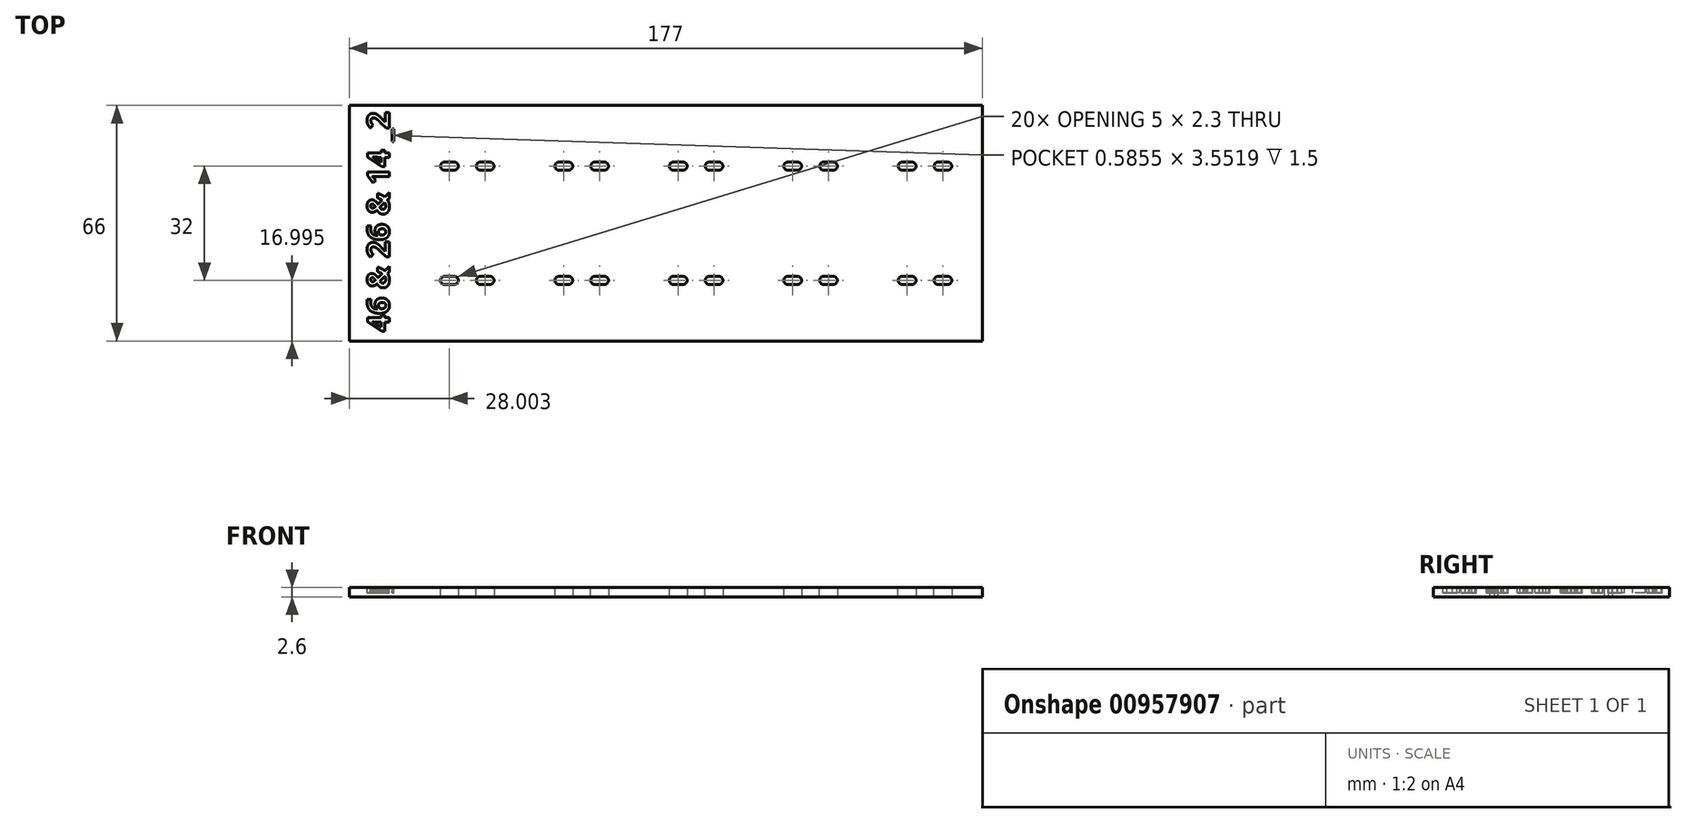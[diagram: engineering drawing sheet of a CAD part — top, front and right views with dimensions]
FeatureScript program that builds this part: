
annotation { "Feature Type Name" : "Feature", "Feature Type Description" : "" }
export const myFeature = defineFeature(function(context is Context, id is Id, definition is map)
    precondition{}
    {
        {
            var Q0;
            Q0=qCreatedBy(makeId("Top.planeOp"),FACE);
            var sketch = newSketch(context, id + "F0", { "sketchPlane" : qUnion([Q0])});
            skLineSegment(sketch, "E0.bottom", {"start": v(-87.55, 16.72) * mm, "end": v(89.45, 16.72) * mm});
            skLineSegment(sketch, "E0.top", {"start": v(-87.55, -49.28) * mm, "end": v(89.45, -49.28) * mm});
            skLineSegment(sketch, "E0.left", {"start": v(-87.55, 16.72) * mm, "end": v(-87.55, -49.28) * mm});
            skLineSegment(sketch, "E0.right", {"start": v(89.45, 16.72) * mm, "end": v(89.45, -49.28) * mm});
            skSolve(sketch);
        }
        {
            var Q0;
            Q0=makeQuery(id+"F0.imprint","IMPRINT",FACE,{"disambiguationData":[TD([[makeQuery(id+"F0.imprint","IMPRINT",EDGE,{"derivedFrom":sQuery(id+"F0.wireOp",EDGE,"E0.bottom")}),-1.0]])]});
            extrude(context, id + "F1", {"entities" : qUnion([Q0]), "depth" : 2.6 * mm, "offsetDistance" : 25 * mm});
        }
        {
            var Q0;
            Q0=makeQuery(id+"F1.opExtrude","CAP_FACE",FACE,{"disambiguationData":[OSD([sQuery(id+"F0.wireOp",EDGE,"E0.bottom"),sQuery(id+"F0.wireOp",EDGE,"E0.top"),sQuery(id+"F0.wireOp",EDGE,"E0.left"),sQuery(id+"F0.wireOp",EDGE,"E0.right")])],"isStart":false});
            var sketch = newSketch(context, id + "F2", { "sketchPlane" : qUnion([Q0])});
            skText(sketch, "E1", { "text": "46 & 26 & 14 _2", "fontName": "OpenSans-Bold.ttf"});
            const initialGuessF2  = {"E1": [-0.0764, -0.0467, 0, 1, 0.00616]};
            skSetInitialGuess(sketch, initialGuessF2);
            skSolve(sketch);
        }
        {
            var Q0;
            Q0=qSketchRegion(id+"F2",true);
            extrude(context, id + "F3", {"entities" : qUnion([Q0]), "operationType" : NewBodyOperationType.REMOVE, "oppositeDirection" : true, "depth" : 1.5 * mm, "offsetDistance" : 25 * mm});
        }
        {
            var Q0;
            {var subQ0=sQuery(id+"F0.wireOp",EDGE,"E0.left");var subQ1=sQuery(id+"F0.wireOp",EDGE,"E0.bottom");var subQ2=sQuery(id+"F0.wireOp",EDGE,"E0.right");var subQ3=sQuery(id+"F0.wireOp",EDGE,"E0.top");Q0=makeQuery(id+"F3.boolean.opBoolean","SPLIT",FACE,{"disambiguationData":[TD([makeQuery(id+"F1.opExtrude","SWEPT_FACE",FACE,{"disambiguationData":[OSD([subQ1])]})])],"derivedFrom":makeQuery(id+"F1.opExtrude","CAP_FACE",FACE,{"disambiguationData":[OSD([subQ1,subQ3,subQ0,subQ2])],"isStart":false})});}
            var sketch = newSketch(context, id + "F4", { "sketchPlane" : qUnion([Q0])});
            skCircle(sketch, "E2", {"center": v(-59.55, -0.28) * mm, "radius": 1.15 * mm});
            skCircle(sketch, "E3", {"center": v(-49.55, -0.28) * mm, "radius": 1.15 * mm});
            skCircle(sketch, "E4", {"center": v(-27.55, -0.28) * mm, "radius": 1.15 * mm});
            skCircle(sketch, "E5", {"center": v(-17.55, -0.28) * mm, "radius": 1.15 * mm});
            skCircle(sketch, "E6", {"center": v(4.45, -0.28) * mm, "radius": 1.15 * mm});
            skCircle(sketch, "E7", {"center": v(14.45, -0.28) * mm, "radius": 1.15 * mm});
            skCircle(sketch, "E8", {"center": v(36.45, -0.28) * mm, "radius": 1.15 * mm});
            skCircle(sketch, "E9", {"center": v(46.45, -0.28) * mm, "radius": 1.15 * mm});
            skCircle(sketch, "E10", {"center": v(68.45, -0.28) * mm, "radius": 1.15 * mm});
            skCircle(sketch, "E11", {"center": v(78.45, -0.28) * mm, "radius": 1.15 * mm});
            skCircle(sketch, "E12", {"center": v(-59.55, -32.28) * mm, "radius": 1.15 * mm});
            skCircle(sketch, "E13", {"center": v(-49.55, -32.28) * mm, "radius": 1.15 * mm});
            skCircle(sketch, "E14", {"center": v(-27.55, -32.28) * mm, "radius": 1.15 * mm});
            skCircle(sketch, "E15", {"center": v(-17.55, -32.28) * mm, "radius": 1.15 * mm});
            skCircle(sketch, "E16", {"center": v(4.45, -32.28) * mm, "radius": 1.15 * mm});
            skCircle(sketch, "E17", {"center": v(14.45, -32.28) * mm, "radius": 1.15 * mm});
            skCircle(sketch, "E18", {"center": v(36.45, -32.28) * mm, "radius": 1.15 * mm});
            skCircle(sketch, "E19", {"center": v(46.45, -32.28) * mm, "radius": 1.15 * mm});
            skCircle(sketch, "E20", {"center": v(68.45, -32.28) * mm, "radius": 1.15 * mm});
            skCircle(sketch, "E21", {"center": v(78.45, -32.28) * mm, "radius": 1.15 * mm});
            skLineSegment(sketch, "E22.bottom", {"start": v(-62.05, -31.13) * mm, "end": v(-57.05, -31.13) * mm});
            skLineSegment(sketch, "E22.top", {"start": v(-62.05, -33.43) * mm, "end": v(-57.05, -33.43) * mm});
            skLineSegment(sketch, "E22.left", {"start": v(-62.05, -31.13) * mm, "end": v(-62.05, -33.43) * mm});
            skLineSegment(sketch, "E22.right", {"start": v(-57.05, -31.13) * mm, "end": v(-57.05, -33.43) * mm});
            skLineSegment(sketch, "E23.bottom", {"start": v(-62.05, 0.87) * mm, "end": v(-57.05, 0.87) * mm});
            skLineSegment(sketch, "E23.top", {"start": v(-62.05, -1.43) * mm, "end": v(-57.05, -1.43) * mm});
            skLineSegment(sketch, "E23.left", {"start": v(-62.05, 0.87) * mm, "end": v(-62.05, -1.43) * mm});
            skLineSegment(sketch, "E23.right", {"start": v(-57.05, 0.87) * mm, "end": v(-57.05, -1.43) * mm});
            skLineSegment(sketch, "E24.bottom", {"start": v(-52.05, 0.87) * mm, "end": v(-47.05, 0.87) * mm});
            skLineSegment(sketch, "E24.top", {"start": v(-52.05, -1.43) * mm, "end": v(-47.05, -1.43) * mm});
            skLineSegment(sketch, "E24.left", {"start": v(-52.05, 0.87) * mm, "end": v(-52.05, -1.43) * mm});
            skLineSegment(sketch, "E24.right", {"start": v(-47.05, 0.87) * mm, "end": v(-47.05, -1.43) * mm});
            skLineSegment(sketch, "E25.bottom", {"start": v(-30.05, 0.87) * mm, "end": v(-25.05, 0.87) * mm});
            skLineSegment(sketch, "E25.top", {"start": v(-30.05, -1.43) * mm, "end": v(-25.05, -1.43) * mm});
            skLineSegment(sketch, "E25.left", {"start": v(-30.05, 0.87) * mm, "end": v(-30.05, -1.43) * mm});
            skLineSegment(sketch, "E25.right", {"start": v(-25.05, 0.87) * mm, "end": v(-25.05, -1.43) * mm});
            skLineSegment(sketch, "E26.bottom", {"start": v(-20.05, 0.87) * mm, "end": v(-15.05, 0.87) * mm});
            skLineSegment(sketch, "E26.top", {"start": v(-20.05, -1.43) * mm, "end": v(-15.05, -1.43) * mm});
            skLineSegment(sketch, "E26.left", {"start": v(-20.05, 0.87) * mm, "end": v(-20.05, -1.43) * mm});
            skLineSegment(sketch, "E26.right", {"start": v(-15.05, 0.87) * mm, "end": v(-15.05, -1.43) * mm});
            skLineSegment(sketch, "E27.bottom", {"start": v(1.95, 0.87) * mm, "end": v(6.95, 0.87) * mm});
            skLineSegment(sketch, "E27.top", {"start": v(1.95, -1.43) * mm, "end": v(6.95, -1.43) * mm});
            skLineSegment(sketch, "E27.left", {"start": v(1.95, 0.87) * mm, "end": v(1.95, -1.43) * mm});
            skLineSegment(sketch, "E27.right", {"start": v(6.95, 0.87) * mm, "end": v(6.95, -1.43) * mm});
            skLineSegment(sketch, "E28.bottom", {"start": v(11.95, 0.87) * mm, "end": v(16.95, 0.87) * mm});
            skLineSegment(sketch, "E28.top", {"start": v(11.95, -1.43) * mm, "end": v(16.95, -1.43) * mm});
            skLineSegment(sketch, "E28.left", {"start": v(11.95, 0.87) * mm, "end": v(11.95, -1.43) * mm});
            skLineSegment(sketch, "E28.right", {"start": v(16.95, 0.87) * mm, "end": v(16.95, -1.43) * mm});
            skLineSegment(sketch, "E29.bottom", {"start": v(33.95, 0.87) * mm, "end": v(38.95, 0.87) * mm});
            skLineSegment(sketch, "E29.top", {"start": v(33.95, -1.43) * mm, "end": v(38.95, -1.43) * mm});
            skLineSegment(sketch, "E29.left", {"start": v(33.95, 0.87) * mm, "end": v(33.95, -1.43) * mm});
            skLineSegment(sketch, "E29.right", {"start": v(38.95, 0.87) * mm, "end": v(38.95, -1.43) * mm});
            skLineSegment(sketch, "E30.bottom", {"start": v(43.95, 0.87) * mm, "end": v(48.95, 0.87) * mm});
            skLineSegment(sketch, "E30.top", {"start": v(43.95, -1.43) * mm, "end": v(48.95, -1.43) * mm});
            skLineSegment(sketch, "E30.left", {"start": v(43.95, 0.87) * mm, "end": v(43.95, -1.43) * mm});
            skLineSegment(sketch, "E30.right", {"start": v(48.95, 0.87) * mm, "end": v(48.95, -1.43) * mm});
            skLineSegment(sketch, "E31.bottom", {"start": v(65.95, 0.87) * mm, "end": v(70.95, 0.87) * mm});
            skLineSegment(sketch, "E31.top", {"start": v(65.95, -1.43) * mm, "end": v(70.95, -1.43) * mm});
            skLineSegment(sketch, "E31.left", {"start": v(65.95, 0.87) * mm, "end": v(65.95, -1.43) * mm});
            skLineSegment(sketch, "E31.right", {"start": v(70.95, 0.87) * mm, "end": v(70.95, -1.43) * mm});
            skLineSegment(sketch, "E32.bottom", {"start": v(75.95, 0.87) * mm, "end": v(80.95, 0.87) * mm});
            skLineSegment(sketch, "E32.top", {"start": v(75.95, -1.43) * mm, "end": v(80.95, -1.43) * mm});
            skLineSegment(sketch, "E32.left", {"start": v(75.95, 0.87) * mm, "end": v(75.95, -1.43) * mm});
            skLineSegment(sketch, "E32.right", {"start": v(80.95, 0.87) * mm, "end": v(80.95, -1.43) * mm});
            skLineSegment(sketch, "E33.bottom", {"start": v(-52.05, -31.13) * mm, "end": v(-47.05, -31.13) * mm});
            skLineSegment(sketch, "E33.top", {"start": v(-52.05, -33.43) * mm, "end": v(-47.05, -33.43) * mm});
            skLineSegment(sketch, "E33.left", {"start": v(-52.05, -31.13) * mm, "end": v(-52.05, -33.43) * mm});
            skLineSegment(sketch, "E33.right", {"start": v(-47.05, -31.13) * mm, "end": v(-47.05, -33.43) * mm});
            skLineSegment(sketch, "E34.bottom", {"start": v(-30.05, -31.13) * mm, "end": v(-25.05, -31.13) * mm});
            skLineSegment(sketch, "E34.top", {"start": v(-30.05, -33.43) * mm, "end": v(-25.05, -33.43) * mm});
            skLineSegment(sketch, "E34.left", {"start": v(-30.05, -31.13) * mm, "end": v(-30.05, -33.43) * mm});
            skLineSegment(sketch, "E34.right", {"start": v(-25.05, -31.13) * mm, "end": v(-25.05, -33.43) * mm});
            skLineSegment(sketch, "E35.bottom", {"start": v(-20.05, -31.13) * mm, "end": v(-15.05, -31.13) * mm});
            skLineSegment(sketch, "E35.top", {"start": v(-20.05, -33.43) * mm, "end": v(-15.05, -33.43) * mm});
            skLineSegment(sketch, "E35.left", {"start": v(-20.05, -31.13) * mm, "end": v(-20.05, -33.43) * mm});
            skLineSegment(sketch, "E35.right", {"start": v(-15.05, -31.13) * mm, "end": v(-15.05, -33.43) * mm});
            skLineSegment(sketch, "E36.bottom", {"start": v(1.95, -31.13) * mm, "end": v(6.95, -31.13) * mm});
            skLineSegment(sketch, "E36.top", {"start": v(1.95, -33.43) * mm, "end": v(6.95, -33.43) * mm});
            skLineSegment(sketch, "E36.left", {"start": v(1.95, -31.13) * mm, "end": v(1.95, -33.43) * mm});
            skLineSegment(sketch, "E36.right", {"start": v(6.95, -31.13) * mm, "end": v(6.95, -33.43) * mm});
            skLineSegment(sketch, "E37.bottom", {"start": v(11.95, -31.13) * mm, "end": v(16.95, -31.13) * mm});
            skLineSegment(sketch, "E37.top", {"start": v(11.95, -33.43) * mm, "end": v(16.95, -33.43) * mm});
            skLineSegment(sketch, "E37.left", {"start": v(11.95, -31.13) * mm, "end": v(11.95, -33.43) * mm});
            skLineSegment(sketch, "E37.right", {"start": v(16.95, -31.13) * mm, "end": v(16.95, -33.43) * mm});
            skLineSegment(sketch, "E38.bottom", {"start": v(33.95, -31.13) * mm, "end": v(38.95, -31.13) * mm});
            skLineSegment(sketch, "E38.top", {"start": v(33.95, -33.43) * mm, "end": v(38.95, -33.43) * mm});
            skLineSegment(sketch, "E38.left", {"start": v(33.95, -31.13) * mm, "end": v(33.95, -33.43) * mm});
            skLineSegment(sketch, "E38.right", {"start": v(38.95, -31.13) * mm, "end": v(38.95, -33.43) * mm});
            skLineSegment(sketch, "E39.bottom", {"start": v(43.95, -31.13) * mm, "end": v(48.95, -31.13) * mm});
            skLineSegment(sketch, "E39.top", {"start": v(43.95, -33.43) * mm, "end": v(48.95, -33.43) * mm});
            skLineSegment(sketch, "E39.left", {"start": v(43.95, -31.13) * mm, "end": v(43.95, -33.43) * mm});
            skLineSegment(sketch, "E39.right", {"start": v(48.95, -31.13) * mm, "end": v(48.95, -33.43) * mm});
            skLineSegment(sketch, "E40.bottom", {"start": v(65.95, -31.13) * mm, "end": v(70.95, -31.13) * mm});
            skLineSegment(sketch, "E40.top", {"start": v(65.95, -33.43) * mm, "end": v(70.95, -33.43) * mm});
            skLineSegment(sketch, "E40.left", {"start": v(65.95, -31.13) * mm, "end": v(65.95, -33.43) * mm});
            skLineSegment(sketch, "E40.right", {"start": v(70.95, -31.13) * mm, "end": v(70.95, -33.43) * mm});
            skLineSegment(sketch, "E41.bottom", {"start": v(75.95, -31.13) * mm, "end": v(80.95, -31.13) * mm});
            skLineSegment(sketch, "E41.top", {"start": v(75.95, -33.43) * mm, "end": v(80.95, -33.43) * mm});
            skLineSegment(sketch, "E41.left", {"start": v(75.95, -31.13) * mm, "end": v(75.95, -33.43) * mm});
            skLineSegment(sketch, "E41.right", {"start": v(80.95, -31.13) * mm, "end": v(80.95, -33.43) * mm});
            skSolve(sketch);
        }
        {
            var Q0;
            Q0=qSketchRegion(id+"F4",true);
            extrude(context, id + "F5", {"entities" : qUnion([Q0]), "operationType" : NewBodyOperationType.REMOVE, "endBound" : BoundingType.UP_TO_NEXT, "oppositeDirection" : true, "depth" : 25 * mm, "offsetDistance" : 25 * mm});
        }
        {
            var Q0;
            Q0=makeQuery(id+"F5.boolean.opBoolean","COPY",EDGE,{"derivedFrom":makeQuery(id+"F5.opExtrude","SWEPT_EDGE",EDGE,{"disambiguationData":[OSD([sQuery(id+"F4.wireOp",EDGE,"E23.bottom"),sQuery(id+"F4.wireOp",EDGE,"E23.left")])]})});
            var Q1;
            Q1=makeQuery(id+"F5.boolean.opBoolean","COPY",EDGE,{"derivedFrom":makeQuery(id+"F5.opExtrude","SWEPT_EDGE",EDGE,{"disambiguationData":[OSD([sQuery(id+"F4.wireOp",EDGE,"E24.bottom"),sQuery(id+"F4.wireOp",EDGE,"E24.left")])]})});
            var Q2;
            Q2=makeQuery(id+"F5.boolean.opBoolean","COPY",EDGE,{"derivedFrom":makeQuery(id+"F5.opExtrude","SWEPT_EDGE",EDGE,{"disambiguationData":[OSD([sQuery(id+"F4.wireOp",EDGE,"E25.bottom"),sQuery(id+"F4.wireOp",EDGE,"E25.left")])]})});
            var Q3;
            Q3=makeQuery(id+"F5.boolean.opBoolean","COPY",EDGE,{"derivedFrom":makeQuery(id+"F5.opExtrude","SWEPT_EDGE",EDGE,{"disambiguationData":[OSD([sQuery(id+"F4.wireOp",EDGE,"E26.bottom"),sQuery(id+"F4.wireOp",EDGE,"E26.left")])]})});
            var Q4;
            Q4=makeQuery(id+"F5.boolean.opBoolean","COPY",EDGE,{"derivedFrom":makeQuery(id+"F5.opExtrude","SWEPT_EDGE",EDGE,{"disambiguationData":[OSD([sQuery(id+"F4.wireOp",EDGE,"E27.bottom"),sQuery(id+"F4.wireOp",EDGE,"E27.left")])]})});
            var Q5;
            Q5=makeQuery(id+"F5.boolean.opBoolean","COPY",EDGE,{"derivedFrom":makeQuery(id+"F5.opExtrude","SWEPT_EDGE",EDGE,{"disambiguationData":[OSD([sQuery(id+"F4.wireOp",EDGE,"E28.bottom"),sQuery(id+"F4.wireOp",EDGE,"E28.left")])]})});
            var Q6;
            Q6=makeQuery(id+"F5.boolean.opBoolean","COPY",EDGE,{"derivedFrom":makeQuery(id+"F5.opExtrude","SWEPT_EDGE",EDGE,{"disambiguationData":[OSD([sQuery(id+"F4.wireOp",EDGE,"E29.bottom"),sQuery(id+"F4.wireOp",EDGE,"E29.left")])]})});
            var Q7;
            Q7=makeQuery(id+"F5.boolean.opBoolean","COPY",EDGE,{"derivedFrom":makeQuery(id+"F5.opExtrude","SWEPT_EDGE",EDGE,{"disambiguationData":[OSD([sQuery(id+"F4.wireOp",EDGE,"E30.bottom"),sQuery(id+"F4.wireOp",EDGE,"E30.left")])]})});
            var Q8;
            Q8=makeQuery(id+"F5.boolean.opBoolean","COPY",EDGE,{"derivedFrom":makeQuery(id+"F5.opExtrude","SWEPT_EDGE",EDGE,{"disambiguationData":[OSD([sQuery(id+"F4.wireOp",EDGE,"E31.bottom"),sQuery(id+"F4.wireOp",EDGE,"E31.left")])]})});
            var Q9;
            Q9=makeQuery(id+"F5.boolean.opBoolean","COPY",EDGE,{"derivedFrom":makeQuery(id+"F5.opExtrude","SWEPT_EDGE",EDGE,{"disambiguationData":[OSD([sQuery(id+"F4.wireOp",EDGE,"E32.bottom"),sQuery(id+"F4.wireOp",EDGE,"E32.left")])]})});
            var Q10;
            Q10=makeQuery(id+"F5.boolean.opBoolean","COPY",EDGE,{"derivedFrom":makeQuery(id+"F5.opExtrude","SWEPT_EDGE",EDGE,{"disambiguationData":[OSD([sQuery(id+"F4.wireOp",EDGE,"E41.bottom"),sQuery(id+"F4.wireOp",EDGE,"E41.left")])]})});
            var Q11;
            Q11=makeQuery(id+"F5.boolean.opBoolean","COPY",EDGE,{"derivedFrom":makeQuery(id+"F5.opExtrude","SWEPT_EDGE",EDGE,{"disambiguationData":[OSD([sQuery(id+"F4.wireOp",EDGE,"E40.bottom"),sQuery(id+"F4.wireOp",EDGE,"E40.left")])]})});
            var Q12;
            Q12=makeQuery(id+"F5.boolean.opBoolean","COPY",EDGE,{"derivedFrom":makeQuery(id+"F5.opExtrude","SWEPT_EDGE",EDGE,{"disambiguationData":[OSD([sQuery(id+"F4.wireOp",EDGE,"E39.bottom"),sQuery(id+"F4.wireOp",EDGE,"E39.left")])]})});
            var Q13;
            Q13=makeQuery(id+"F5.boolean.opBoolean","COPY",EDGE,{"derivedFrom":makeQuery(id+"F5.opExtrude","SWEPT_EDGE",EDGE,{"disambiguationData":[OSD([sQuery(id+"F4.wireOp",EDGE,"E34.bottom"),sQuery(id+"F4.wireOp",EDGE,"E34.left")])]})});
            var Q14;
            Q14=makeQuery(id+"F5.boolean.opBoolean","COPY",EDGE,{"derivedFrom":makeQuery(id+"F5.opExtrude","SWEPT_EDGE",EDGE,{"disambiguationData":[OSD([sQuery(id+"F4.wireOp",EDGE,"E35.bottom"),sQuery(id+"F4.wireOp",EDGE,"E35.left")])]})});
            var Q15;
            Q15=makeQuery(id+"F5.boolean.opBoolean","COPY",EDGE,{"derivedFrom":makeQuery(id+"F5.opExtrude","SWEPT_EDGE",EDGE,{"disambiguationData":[OSD([sQuery(id+"F4.wireOp",EDGE,"E36.bottom"),sQuery(id+"F4.wireOp",EDGE,"E36.left")])]})});
            var Q16;
            Q16=makeQuery(id+"F5.boolean.opBoolean","COPY",EDGE,{"derivedFrom":makeQuery(id+"F5.opExtrude","SWEPT_EDGE",EDGE,{"disambiguationData":[OSD([sQuery(id+"F4.wireOp",EDGE,"E37.bottom"),sQuery(id+"F4.wireOp",EDGE,"E37.left")])]})});
            var Q17;
            Q17=makeQuery(id+"F5.boolean.opBoolean","COPY",EDGE,{"derivedFrom":makeQuery(id+"F5.opExtrude","SWEPT_EDGE",EDGE,{"disambiguationData":[OSD([sQuery(id+"F4.wireOp",EDGE,"E38.bottom"),sQuery(id+"F4.wireOp",EDGE,"E38.left")])]})});
            var Q18;
            Q18=makeQuery(id+"F5.boolean.opBoolean","COPY",EDGE,{"derivedFrom":makeQuery(id+"F5.opExtrude","SWEPT_EDGE",EDGE,{"disambiguationData":[OSD([sQuery(id+"F4.wireOp",EDGE,"E22.bottom"),sQuery(id+"F4.wireOp",EDGE,"E22.left")])]})});
            var Q19;
            Q19=makeQuery(id+"F5.boolean.opBoolean","COPY",EDGE,{"derivedFrom":makeQuery(id+"F5.opExtrude","SWEPT_EDGE",EDGE,{"disambiguationData":[OSD([sQuery(id+"F4.wireOp",EDGE,"E33.bottom"),sQuery(id+"F4.wireOp",EDGE,"E33.left")])]})});
            var Q20;
            Q20=makeQuery(id+"F5.boolean.opBoolean","COPY",EDGE,{"derivedFrom":makeQuery(id+"F5.opExtrude","SWEPT_EDGE",EDGE,{"disambiguationData":[OSD([sQuery(id+"F4.wireOp",EDGE,"E23.bottom"),sQuery(id+"F4.wireOp",EDGE,"E23.right")])]})});
            var Q21;
            Q21=makeQuery(id+"F5.boolean.opBoolean","COPY",EDGE,{"derivedFrom":makeQuery(id+"F5.opExtrude","SWEPT_EDGE",EDGE,{"disambiguationData":[OSD([sQuery(id+"F4.wireOp",EDGE,"E24.bottom"),sQuery(id+"F4.wireOp",EDGE,"E24.right")])]})});
            var Q22;
            Q22=makeQuery(id+"F5.boolean.opBoolean","COPY",EDGE,{"derivedFrom":makeQuery(id+"F5.opExtrude","SWEPT_EDGE",EDGE,{"disambiguationData":[OSD([sQuery(id+"F4.wireOp",EDGE,"E25.bottom"),sQuery(id+"F4.wireOp",EDGE,"E25.right")])]})});
            var Q23;
            Q23=makeQuery(id+"F5.boolean.opBoolean","COPY",EDGE,{"derivedFrom":makeQuery(id+"F5.opExtrude","SWEPT_EDGE",EDGE,{"disambiguationData":[OSD([sQuery(id+"F4.wireOp",EDGE,"E26.bottom"),sQuery(id+"F4.wireOp",EDGE,"E26.right")])]})});
            var Q24;
            Q24=makeQuery(id+"F5.boolean.opBoolean","COPY",EDGE,{"derivedFrom":makeQuery(id+"F5.opExtrude","SWEPT_EDGE",EDGE,{"disambiguationData":[OSD([sQuery(id+"F4.wireOp",EDGE,"E27.bottom"),sQuery(id+"F4.wireOp",EDGE,"E27.right")])]})});
            var Q25;
            Q25=makeQuery(id+"F5.boolean.opBoolean","COPY",EDGE,{"derivedFrom":makeQuery(id+"F5.opExtrude","SWEPT_EDGE",EDGE,{"disambiguationData":[OSD([sQuery(id+"F4.wireOp",EDGE,"E28.bottom"),sQuery(id+"F4.wireOp",EDGE,"E28.right")])]})});
            var Q26;
            Q26=makeQuery(id+"F5.boolean.opBoolean","COPY",EDGE,{"derivedFrom":makeQuery(id+"F5.opExtrude","SWEPT_EDGE",EDGE,{"disambiguationData":[OSD([sQuery(id+"F4.wireOp",EDGE,"E29.bottom"),sQuery(id+"F4.wireOp",EDGE,"E29.right")])]})});
            var Q27;
            Q27=makeQuery(id+"F5.boolean.opBoolean","COPY",EDGE,{"derivedFrom":makeQuery(id+"F5.opExtrude","SWEPT_EDGE",EDGE,{"disambiguationData":[OSD([sQuery(id+"F4.wireOp",EDGE,"E30.bottom"),sQuery(id+"F4.wireOp",EDGE,"E30.right")])]})});
            var Q28;
            Q28=makeQuery(id+"F5.boolean.opBoolean","COPY",EDGE,{"derivedFrom":makeQuery(id+"F5.opExtrude","SWEPT_EDGE",EDGE,{"disambiguationData":[OSD([sQuery(id+"F4.wireOp",EDGE,"E31.bottom"),sQuery(id+"F4.wireOp",EDGE,"E31.right")])]})});
            var Q29;
            Q29=makeQuery(id+"F5.boolean.opBoolean","COPY",EDGE,{"derivedFrom":makeQuery(id+"F5.opExtrude","SWEPT_EDGE",EDGE,{"disambiguationData":[OSD([sQuery(id+"F4.wireOp",EDGE,"E32.bottom"),sQuery(id+"F4.wireOp",EDGE,"E32.right")])]})});
            var Q30;
            Q30=makeQuery(id+"F5.boolean.opBoolean","COPY",EDGE,{"derivedFrom":makeQuery(id+"F5.opExtrude","SWEPT_EDGE",EDGE,{"disambiguationData":[OSD([sQuery(id+"F4.wireOp",EDGE,"E41.bottom"),sQuery(id+"F4.wireOp",EDGE,"E41.right")])]})});
            var Q31;
            Q31=makeQuery(id+"F5.boolean.opBoolean","COPY",EDGE,{"derivedFrom":makeQuery(id+"F5.opExtrude","SWEPT_EDGE",EDGE,{"disambiguationData":[OSD([sQuery(id+"F4.wireOp",EDGE,"E40.bottom"),sQuery(id+"F4.wireOp",EDGE,"E40.right")])]})});
            var Q32;
            Q32=makeQuery(id+"F5.boolean.opBoolean","COPY",EDGE,{"derivedFrom":makeQuery(id+"F5.opExtrude","SWEPT_EDGE",EDGE,{"disambiguationData":[OSD([sQuery(id+"F4.wireOp",EDGE,"E39.bottom"),sQuery(id+"F4.wireOp",EDGE,"E39.right")])]})});
            var Q33;
            Q33=makeQuery(id+"F5.boolean.opBoolean","COPY",EDGE,{"derivedFrom":makeQuery(id+"F5.opExtrude","SWEPT_EDGE",EDGE,{"disambiguationData":[OSD([sQuery(id+"F4.wireOp",EDGE,"E38.bottom"),sQuery(id+"F4.wireOp",EDGE,"E38.right")])]})});
            var Q34;
            Q34=makeQuery(id+"F5.boolean.opBoolean","COPY",EDGE,{"derivedFrom":makeQuery(id+"F5.opExtrude","SWEPT_EDGE",EDGE,{"disambiguationData":[OSD([sQuery(id+"F4.wireOp",EDGE,"E37.bottom"),sQuery(id+"F4.wireOp",EDGE,"E37.right")])]})});
            var Q35;
            Q35=makeQuery(id+"F5.boolean.opBoolean","COPY",EDGE,{"derivedFrom":makeQuery(id+"F5.opExtrude","SWEPT_EDGE",EDGE,{"disambiguationData":[OSD([sQuery(id+"F4.wireOp",EDGE,"E36.bottom"),sQuery(id+"F4.wireOp",EDGE,"E36.right")])]})});
            var Q36;
            Q36=makeQuery(id+"F5.boolean.opBoolean","COPY",EDGE,{"derivedFrom":makeQuery(id+"F5.opExtrude","SWEPT_EDGE",EDGE,{"disambiguationData":[OSD([sQuery(id+"F4.wireOp",EDGE,"E35.bottom"),sQuery(id+"F4.wireOp",EDGE,"E35.right")])]})});
            var Q37;
            Q37=makeQuery(id+"F5.boolean.opBoolean","COPY",EDGE,{"derivedFrom":makeQuery(id+"F5.opExtrude","SWEPT_EDGE",EDGE,{"disambiguationData":[OSD([sQuery(id+"F4.wireOp",EDGE,"E34.bottom"),sQuery(id+"F4.wireOp",EDGE,"E34.right")])]})});
            var Q38;
            Q38=makeQuery(id+"F5.boolean.opBoolean","COPY",EDGE,{"derivedFrom":makeQuery(id+"F5.opExtrude","SWEPT_EDGE",EDGE,{"disambiguationData":[OSD([sQuery(id+"F4.wireOp",EDGE,"E33.bottom"),sQuery(id+"F4.wireOp",EDGE,"E33.right")])]})});
            var Q39;
            Q39=makeQuery(id+"F5.boolean.opBoolean","COPY",EDGE,{"derivedFrom":makeQuery(id+"F5.opExtrude","SWEPT_EDGE",EDGE,{"disambiguationData":[OSD([sQuery(id+"F4.wireOp",EDGE,"E22.bottom"),sQuery(id+"F4.wireOp",EDGE,"E22.right")])]})});
            var Q40;
            Q40=makeQuery(id+"F5.boolean.opBoolean","COPY",EDGE,{"derivedFrom":makeQuery(id+"F5.opExtrude","SWEPT_EDGE",EDGE,{"disambiguationData":[OSD([sQuery(id+"F4.wireOp",EDGE,"E32.top"),sQuery(id+"F4.wireOp",EDGE,"E32.right")])]})});
            var Q41;
            Q41=makeQuery(id+"F5.boolean.opBoolean","COPY",EDGE,{"derivedFrom":makeQuery(id+"F5.opExtrude","SWEPT_EDGE",EDGE,{"disambiguationData":[OSD([sQuery(id+"F4.wireOp",EDGE,"E41.top"),sQuery(id+"F4.wireOp",EDGE,"E41.right")])]})});
            var Q42;
            Q42=makeQuery(id+"F5.boolean.opBoolean","COPY",EDGE,{"derivedFrom":makeQuery(id+"F5.opExtrude","SWEPT_EDGE",EDGE,{"disambiguationData":[OSD([sQuery(id+"F4.wireOp",EDGE,"E31.top"),sQuery(id+"F4.wireOp",EDGE,"E31.right")])]})});
            var Q43;
            Q43=makeQuery(id+"F5.boolean.opBoolean","COPY",EDGE,{"derivedFrom":makeQuery(id+"F5.opExtrude","SWEPT_EDGE",EDGE,{"disambiguationData":[OSD([sQuery(id+"F4.wireOp",EDGE,"E30.top"),sQuery(id+"F4.wireOp",EDGE,"E30.right")])]})});
            var Q44;
            Q44=makeQuery(id+"F5.boolean.opBoolean","COPY",EDGE,{"derivedFrom":makeQuery(id+"F5.opExtrude","SWEPT_EDGE",EDGE,{"disambiguationData":[OSD([sQuery(id+"F4.wireOp",EDGE,"E39.top"),sQuery(id+"F4.wireOp",EDGE,"E39.right")])]})});
            var Q45;
            Q45=makeQuery(id+"F5.boolean.opBoolean","COPY",EDGE,{"derivedFrom":makeQuery(id+"F5.opExtrude","SWEPT_EDGE",EDGE,{"disambiguationData":[OSD([sQuery(id+"F4.wireOp",EDGE,"E38.top"),sQuery(id+"F4.wireOp",EDGE,"E38.right")])]})});
            var Q46;
            Q46=makeQuery(id+"F5.boolean.opBoolean","COPY",EDGE,{"derivedFrom":makeQuery(id+"F5.opExtrude","SWEPT_EDGE",EDGE,{"disambiguationData":[OSD([sQuery(id+"F4.wireOp",EDGE,"E29.top"),sQuery(id+"F4.wireOp",EDGE,"E29.right")])]})});
            var Q47;
            Q47=makeQuery(id+"F5.boolean.opBoolean","COPY",EDGE,{"derivedFrom":makeQuery(id+"F5.opExtrude","SWEPT_EDGE",EDGE,{"disambiguationData":[OSD([sQuery(id+"F4.wireOp",EDGE,"E28.top"),sQuery(id+"F4.wireOp",EDGE,"E28.right")])]})});
            var Q48;
            Q48=makeQuery(id+"F5.boolean.opBoolean","COPY",EDGE,{"derivedFrom":makeQuery(id+"F5.opExtrude","SWEPT_EDGE",EDGE,{"disambiguationData":[OSD([sQuery(id+"F4.wireOp",EDGE,"E27.top"),sQuery(id+"F4.wireOp",EDGE,"E27.right")])]})});
            var Q49;
            Q49=makeQuery(id+"F5.boolean.opBoolean","COPY",EDGE,{"derivedFrom":makeQuery(id+"F5.opExtrude","SWEPT_EDGE",EDGE,{"disambiguationData":[OSD([sQuery(id+"F4.wireOp",EDGE,"E26.top"),sQuery(id+"F4.wireOp",EDGE,"E26.right")])]})});
            var Q50;
            Q50=makeQuery(id+"F5.boolean.opBoolean","COPY",EDGE,{"derivedFrom":makeQuery(id+"F5.opExtrude","SWEPT_EDGE",EDGE,{"disambiguationData":[OSD([sQuery(id+"F4.wireOp",EDGE,"E25.top"),sQuery(id+"F4.wireOp",EDGE,"E25.right")])]})});
            var Q51;
            Q51=makeQuery(id+"F5.boolean.opBoolean","COPY",EDGE,{"derivedFrom":makeQuery(id+"F5.opExtrude","SWEPT_EDGE",EDGE,{"disambiguationData":[OSD([sQuery(id+"F4.wireOp",EDGE,"E37.top"),sQuery(id+"F4.wireOp",EDGE,"E37.right")])]})});
            var Q52;
            Q52=makeQuery(id+"F5.boolean.opBoolean","COPY",EDGE,{"derivedFrom":makeQuery(id+"F5.opExtrude","SWEPT_EDGE",EDGE,{"disambiguationData":[OSD([sQuery(id+"F4.wireOp",EDGE,"E36.top"),sQuery(id+"F4.wireOp",EDGE,"E36.right")])]})});
            var Q53;
            Q53=makeQuery(id+"F5.boolean.opBoolean","COPY",EDGE,{"derivedFrom":makeQuery(id+"F5.opExtrude","SWEPT_EDGE",EDGE,{"disambiguationData":[OSD([sQuery(id+"F4.wireOp",EDGE,"E35.top"),sQuery(id+"F4.wireOp",EDGE,"E35.right")])]})});
            var Q54;
            Q54=makeQuery(id+"F5.boolean.opBoolean","COPY",EDGE,{"derivedFrom":makeQuery(id+"F5.opExtrude","SWEPT_EDGE",EDGE,{"disambiguationData":[OSD([sQuery(id+"F4.wireOp",EDGE,"E34.top"),sQuery(id+"F4.wireOp",EDGE,"E34.right")])]})});
            var Q55;
            Q55=makeQuery(id+"F5.boolean.opBoolean","COPY",EDGE,{"derivedFrom":makeQuery(id+"F5.opExtrude","SWEPT_EDGE",EDGE,{"disambiguationData":[OSD([sQuery(id+"F4.wireOp",EDGE,"E33.top"),sQuery(id+"F4.wireOp",EDGE,"E33.right")])]})});
            var Q56;
            Q56=makeQuery(id+"F5.boolean.opBoolean","COPY",EDGE,{"derivedFrom":makeQuery(id+"F5.opExtrude","SWEPT_EDGE",EDGE,{"disambiguationData":[OSD([sQuery(id+"F4.wireOp",EDGE,"E22.top"),sQuery(id+"F4.wireOp",EDGE,"E22.right")])]})});
            var Q57;
            Q57=makeQuery(id+"F5.boolean.opBoolean","COPY",EDGE,{"derivedFrom":makeQuery(id+"F5.opExtrude","SWEPT_EDGE",EDGE,{"disambiguationData":[OSD([sQuery(id+"F4.wireOp",EDGE,"E23.top"),sQuery(id+"F4.wireOp",EDGE,"E23.right")])]})});
            var Q58;
            Q58=makeQuery(id+"F5.boolean.opBoolean","COPY",EDGE,{"derivedFrom":makeQuery(id+"F5.opExtrude","SWEPT_EDGE",EDGE,{"disambiguationData":[OSD([sQuery(id+"F4.wireOp",EDGE,"E24.top"),sQuery(id+"F4.wireOp",EDGE,"E24.right")])]})});
            var Q59;
            Q59=makeQuery(id+"F5.boolean.opBoolean","COPY",EDGE,{"derivedFrom":makeQuery(id+"F5.opExtrude","SWEPT_EDGE",EDGE,{"disambiguationData":[OSD([sQuery(id+"F4.wireOp",EDGE,"E41.top"),sQuery(id+"F4.wireOp",EDGE,"E41.left")])]})});
            var Q60;
            Q60=makeQuery(id+"F5.boolean.opBoolean","COPY",EDGE,{"derivedFrom":makeQuery(id+"F5.opExtrude","SWEPT_EDGE",EDGE,{"disambiguationData":[OSD([sQuery(id+"F4.wireOp",EDGE,"E40.top"),sQuery(id+"F4.wireOp",EDGE,"E40.left")])]})});
            var Q61;
            Q61=makeQuery(id+"F5.boolean.opBoolean","COPY",EDGE,{"derivedFrom":makeQuery(id+"F5.opExtrude","SWEPT_EDGE",EDGE,{"disambiguationData":[OSD([sQuery(id+"F4.wireOp",EDGE,"E32.top"),sQuery(id+"F4.wireOp",EDGE,"E32.left")])]})});
            var Q62;
            Q62=makeQuery(id+"F5.boolean.opBoolean","COPY",EDGE,{"derivedFrom":makeQuery(id+"F5.opExtrude","SWEPT_EDGE",EDGE,{"disambiguationData":[OSD([sQuery(id+"F4.wireOp",EDGE,"E31.top"),sQuery(id+"F4.wireOp",EDGE,"E31.left")])]})});
            var Q63;
            Q63=makeQuery(id+"F5.boolean.opBoolean","COPY",EDGE,{"derivedFrom":makeQuery(id+"F5.opExtrude","SWEPT_EDGE",EDGE,{"disambiguationData":[OSD([sQuery(id+"F4.wireOp",EDGE,"E30.top"),sQuery(id+"F4.wireOp",EDGE,"E30.left")])]})});
            var Q64;
            Q64=makeQuery(id+"F5.boolean.opBoolean","COPY",EDGE,{"derivedFrom":makeQuery(id+"F5.opExtrude","SWEPT_EDGE",EDGE,{"disambiguationData":[OSD([sQuery(id+"F4.wireOp",EDGE,"E29.top"),sQuery(id+"F4.wireOp",EDGE,"E29.left")])]})});
            var Q65;
            Q65=makeQuery(id+"F5.boolean.opBoolean","COPY",EDGE,{"derivedFrom":makeQuery(id+"F5.opExtrude","SWEPT_EDGE",EDGE,{"disambiguationData":[OSD([sQuery(id+"F4.wireOp",EDGE,"E28.top"),sQuery(id+"F4.wireOp",EDGE,"E28.left")])]})});
            var Q66;
            Q66=makeQuery(id+"F5.boolean.opBoolean","COPY",EDGE,{"derivedFrom":makeQuery(id+"F5.opExtrude","SWEPT_EDGE",EDGE,{"disambiguationData":[OSD([sQuery(id+"F4.wireOp",EDGE,"E27.top"),sQuery(id+"F4.wireOp",EDGE,"E27.left")])]})});
            var Q67;
            Q67=makeQuery(id+"F5.boolean.opBoolean","COPY",EDGE,{"derivedFrom":makeQuery(id+"F5.opExtrude","SWEPT_EDGE",EDGE,{"disambiguationData":[OSD([sQuery(id+"F4.wireOp",EDGE,"E26.top"),sQuery(id+"F4.wireOp",EDGE,"E26.left")])]})});
            var Q68;
            Q68=makeQuery(id+"F5.boolean.opBoolean","COPY",EDGE,{"derivedFrom":makeQuery(id+"F5.opExtrude","SWEPT_EDGE",EDGE,{"disambiguationData":[OSD([sQuery(id+"F4.wireOp",EDGE,"E25.top"),sQuery(id+"F4.wireOp",EDGE,"E25.left")])]})});
            var Q69;
            Q69=makeQuery(id+"F5.boolean.opBoolean","COPY",EDGE,{"derivedFrom":makeQuery(id+"F5.opExtrude","SWEPT_EDGE",EDGE,{"disambiguationData":[OSD([sQuery(id+"F4.wireOp",EDGE,"E24.top"),sQuery(id+"F4.wireOp",EDGE,"E24.left")])]})});
            var Q70;
            Q70=makeQuery(id+"F5.boolean.opBoolean","COPY",EDGE,{"derivedFrom":makeQuery(id+"F5.opExtrude","SWEPT_EDGE",EDGE,{"disambiguationData":[OSD([sQuery(id+"F4.wireOp",EDGE,"E23.top"),sQuery(id+"F4.wireOp",EDGE,"E23.left")])]})});
            var Q71;
            Q71=makeQuery(id+"F5.boolean.opBoolean","COPY",EDGE,{"derivedFrom":makeQuery(id+"F5.opExtrude","SWEPT_EDGE",EDGE,{"disambiguationData":[OSD([sQuery(id+"F4.wireOp",EDGE,"E22.top"),sQuery(id+"F4.wireOp",EDGE,"E22.left")])]})});
            var Q72;
            Q72=makeQuery(id+"F5.boolean.opBoolean","COPY",EDGE,{"derivedFrom":makeQuery(id+"F5.opExtrude","SWEPT_EDGE",EDGE,{"disambiguationData":[OSD([sQuery(id+"F4.wireOp",EDGE,"E33.top"),sQuery(id+"F4.wireOp",EDGE,"E33.left")])]})});
            var Q73;
            Q73=makeQuery(id+"F5.boolean.opBoolean","COPY",EDGE,{"derivedFrom":makeQuery(id+"F5.opExtrude","SWEPT_EDGE",EDGE,{"disambiguationData":[OSD([sQuery(id+"F4.wireOp",EDGE,"E34.top"),sQuery(id+"F4.wireOp",EDGE,"E34.left")])]})});
            var Q74;
            Q74=makeQuery(id+"F5.boolean.opBoolean","COPY",EDGE,{"derivedFrom":makeQuery(id+"F5.opExtrude","SWEPT_EDGE",EDGE,{"disambiguationData":[OSD([sQuery(id+"F4.wireOp",EDGE,"E35.top"),sQuery(id+"F4.wireOp",EDGE,"E35.left")])]})});
            var Q75;
            Q75=makeQuery(id+"F5.boolean.opBoolean","COPY",EDGE,{"derivedFrom":makeQuery(id+"F5.opExtrude","SWEPT_EDGE",EDGE,{"disambiguationData":[OSD([sQuery(id+"F4.wireOp",EDGE,"E36.top"),sQuery(id+"F4.wireOp",EDGE,"E36.left")])]})});
            var Q76;
            Q76=makeQuery(id+"F5.boolean.opBoolean","COPY",EDGE,{"derivedFrom":makeQuery(id+"F5.opExtrude","SWEPT_EDGE",EDGE,{"disambiguationData":[OSD([sQuery(id+"F4.wireOp",EDGE,"E37.top"),sQuery(id+"F4.wireOp",EDGE,"E37.left")])]})});
            var Q77;
            Q77=makeQuery(id+"F5.boolean.opBoolean","COPY",EDGE,{"derivedFrom":makeQuery(id+"F5.opExtrude","SWEPT_EDGE",EDGE,{"disambiguationData":[OSD([sQuery(id+"F4.wireOp",EDGE,"E38.top"),sQuery(id+"F4.wireOp",EDGE,"E38.left")])]})});
            var Q78;
            Q78=makeQuery(id+"F5.boolean.opBoolean","COPY",EDGE,{"derivedFrom":makeQuery(id+"F5.opExtrude","SWEPT_EDGE",EDGE,{"disambiguationData":[OSD([sQuery(id+"F4.wireOp",EDGE,"E39.top"),sQuery(id+"F4.wireOp",EDGE,"E39.left")])]})});
            var Q79;
            Q79=makeQuery(id+"F5.boolean.opBoolean","COPY",EDGE,{"derivedFrom":makeQuery(id+"F5.opExtrude","SWEPT_EDGE",EDGE,{"disambiguationData":[OSD([sQuery(id+"F4.wireOp",EDGE,"E40.top"),sQuery(id+"F4.wireOp",EDGE,"E40.right")])]})});
            fillet(context, id + "F6", {"entities" : qUnion([Q0, Q1, Q2, Q3, Q4, Q5, Q6, Q7, Q8, Q9, Q10, Q11, Q12, Q13, Q14, Q15, Q16, Q17, Q18, Q19, Q20, Q21, Q22, Q23, Q24, Q25, Q26, Q27, Q28, Q29, Q30, Q31, Q32, Q33, Q34, Q35, Q36, Q37, Q38, Q39, Q40, Q41, Q42, Q43, Q44, Q45, Q46, Q47, Q48, Q49, Q50, Q51, Q52, Q53, Q54, Q55, Q56, Q57, Q58, Q59, Q60, Q61, Q62, Q63, Q64, Q65, Q66, Q67, Q68, Q69, Q70, Q71, Q72, Q73, Q74, Q75, Q76, Q77, Q78, Q79]), "radius" : 1.2 * mm, "tangentPropagation" : true, "allowEdgeOverflow" : false});
        }
    });
